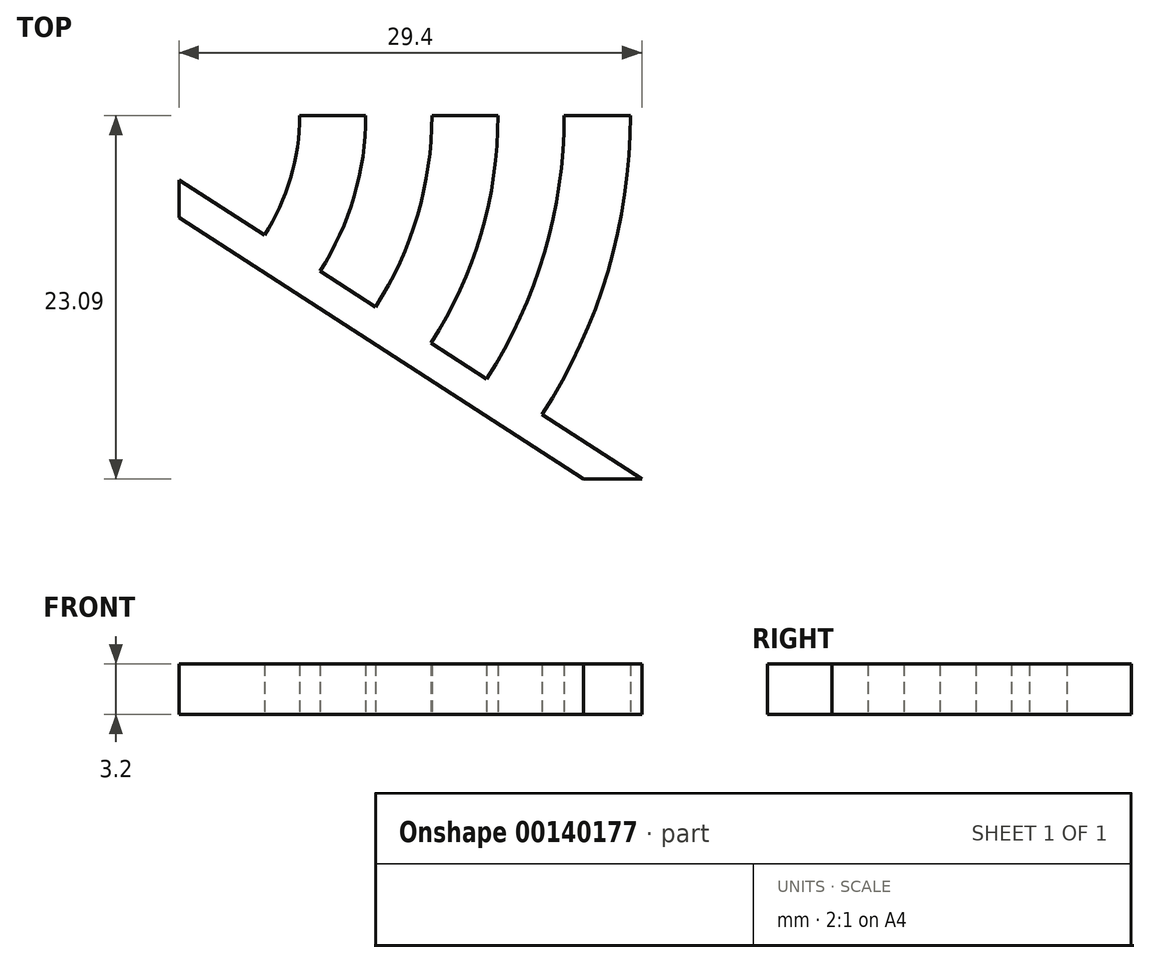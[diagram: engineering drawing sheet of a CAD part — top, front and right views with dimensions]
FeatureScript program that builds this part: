
annotation { "Feature Type Name" : "Feature", "Feature Type Description" : "" }
export const myFeature = defineFeature(function(context is Context, id is Id, definition is map)
    precondition{}
    {
        {
            var Q0;
            Q0=qCreatedBy(makeId("Top.planeOp"),FACE);
            var sketch = newSketch(context, id + "F0", { "sketchPlane" : qUnion([Q0])});
            skLineSegment(sketch, "E0", {"start": v(-29.38, 0.03) * mm, "end": v(-25.18, -2.69) * mm});
            skLineSegment(sketch, "E1", {"start": v(0.02, -18.97) * mm, "end": v(-0.7, -18.5) * mm, "construction": true});
            skLineSegment(sketch, "E2", {"start": v(-29.38, 0.03) * mm, "end": v(-25.18, -2.69) * mm, "construction": true});
            skLineSegment(sketch, "E3", {"start": v(-20.42, -5.76) * mm, "end": v(-16.9, -8.04) * mm, "construction": true});
            skLineSegment(sketch, "E4", {"start": v(-3.67, -18.97) * mm, "end": v(-29.38, -2.36) * mm});
            skLineSegment(sketch, "E5", {"start": v(0.02, -18.97) * mm, "end": v(-3.67, -18.97) * mm});
            skLineSegment(sketch, "E6", {"start": v(-29.38, 0.03) * mm, "end": v(-29.38, -2.36) * mm});
            skLineSegment(sketch, "E7.trimOffspring", {"start": v(-20.42, -5.76) * mm, "end": v(-16.9, -8.04) * mm});
            skLineSegment(sketch, "E8.trimOffspring", {"start": v(-12.59, -10.83) * mm, "end": v(-9.84, -12.6) * mm});
            skLineSegment(sketch, "E9.trimOffspring", {"start": v(-4.18, -16.26) * mm, "end": v(0.02, -18.97) * mm});
            skLineSegment(sketch, "E10", {"start": v(-4.9, 4.12) * mm, "end": v(-0.7, 4.12) * mm});
            skLineSegment(sketch, "E11", {"start": v(-9.11, 4.12) * mm, "end": v(-13.31, 4.12) * mm});
            skLineSegment(sketch, "E12", {"start": v(0.02, -18.97) * mm, "end": v(-29.38, -18.97) * mm, "construction": true});
            skLineSegment(sketch, "E13", {"start": v(-29.38, -18.97) * mm, "end": v(-29.38, 0.03) * mm, "construction": true});
            skLineSegment(sketch, "E14", {"start": v(-0.7, -18.5) * mm, "end": v(-0.7, -18.97) * mm, "construction": true});
            skLineSegment(sketch, "E15", {"start": v(-17.51, 4.12) * mm, "end": v(-29.38, 4.12) * mm, "construction": true});
            skLineSegment(sketch, "E16", {"start": v(-29.38, 0.03) * mm, "end": v(-23.95, -3.48) * mm, "construction": true});
            skLineSegment(sketch, "E17", {"start": v(-29.38, 0.03) * mm, "end": v(-37.37, 5.19) * mm, "construction": true});
            skArc(sketch, "E18", {"start": v(-21.7, 4.12) * mm, "mid": v(-22.28, 0.15) * mm, "end": v(-23.95, -3.48) * mm});
            skArc(sketch, "E19", {"start": v(-13.31, 4.12) * mm, "mid": v(-14.23, -2.22) * mm, "end": v(-16.9, -8.04) * mm});
            skArc(sketch, "E20", {"start": v(-9.11, 4.12) * mm, "mid": v(-10.2, -3.41) * mm, "end": v(-13.37, -10.32) * mm});
            skArc(sketch, "E21", {"start": v(-4.9, 4.12) * mm, "mid": v(-6.17, -4.6) * mm, "end": v(-9.84, -12.6) * mm});
            skArc(sketch, "E22", {"start": v(-0.7, 4.12) * mm, "mid": v(-2.14, -5.79) * mm, "end": v(-6.31, -14.88) * mm});
            skArc(sketch, "E23", {"start": v(-17.51, 4.12) * mm, "mid": v(-18.25, -1.03) * mm, "end": v(-20.42, -5.76) * mm});
            skLineSegment(sketch, "E24", {"start": v(-6.31, -14.88) * mm, "end": v(-4.18, -16.26) * mm});
            skLineSegment(sketch, "E25", {"start": v(-21.7, 4.12) * mm, "end": v(-17.51, 4.12) * mm});
            skLineSegment(sketch, "E26", {"start": v(-25.18, -2.69) * mm, "end": v(-23.95, -3.48) * mm});
            skLineSegment(sketch, "E27.trimOffspring", {"start": v(-13.37, -10.32) * mm, "end": v(-9.84, -12.6) * mm, "construction": true});
            skLineSegment(sketch, "E28", {"start": v(-13.37, -10.32) * mm, "end": v(-12.59, -10.83) * mm});
            skSolve(sketch);
        }
        {
            var Q0;
            Q0=makeQuery(id+"F0.imprint","IMPRINT",FACE,{"disambiguationData":[TD([[makeQuery(id+"F0.imprint","IMPRINT",EDGE,{"derivedFrom":sQuery(id+"F0.wireOp",EDGE,"E0")}),-1.0]])]});
            extrude(context, id + "F1", {"entities" : qUnion([Q0]), "endBound" : BoundingType.SYMMETRIC, "depth" : 3.2 * mm});
        }
    });
